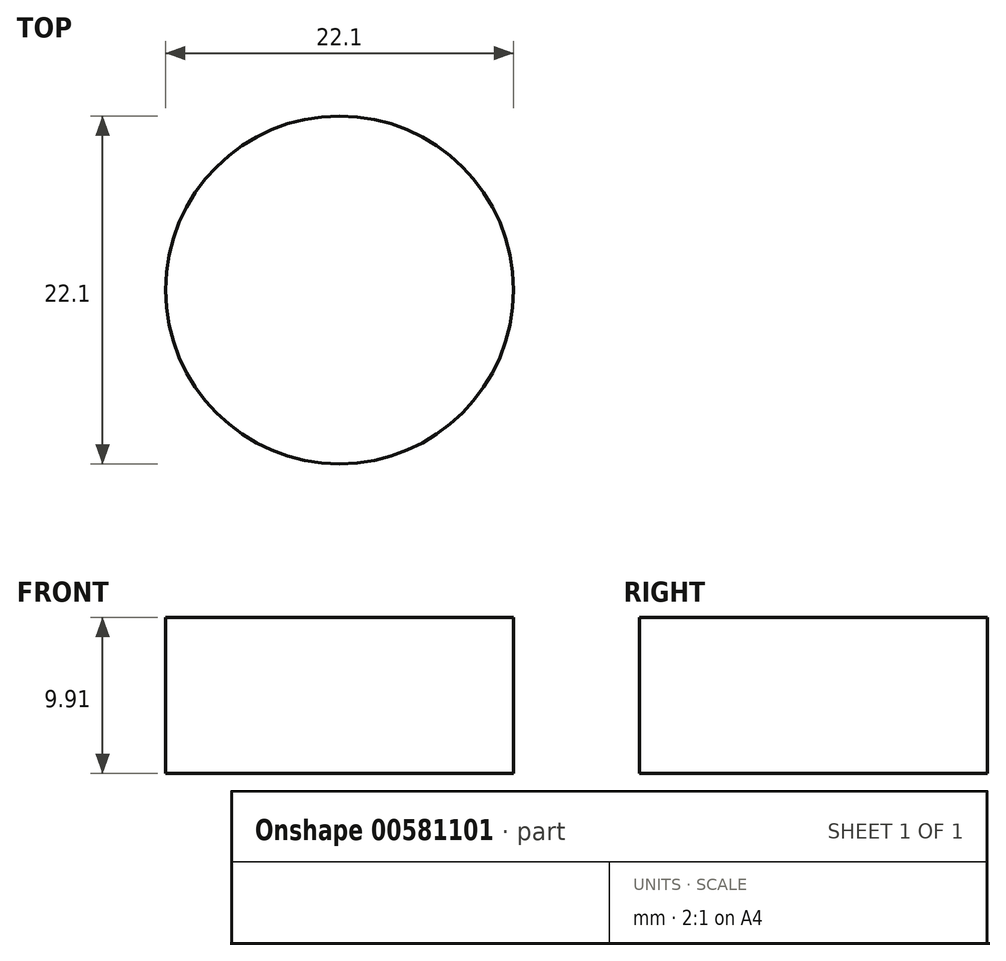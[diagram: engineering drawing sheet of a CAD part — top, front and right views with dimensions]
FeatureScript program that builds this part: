
annotation { "Feature Type Name" : "Feature", "Feature Type Description" : "" }
export const myFeature = defineFeature(function(context is Context, id is Id, definition is map)
    precondition{}
    {
        {
            var Q0;
            Q0=qCreatedBy(makeId("Top.planeOp"),FACE);
            var sketch = newSketch(context, id + "F0", { "sketchPlane" : qUnion([Q0])});
            skCircle(sketch, "E0", {"center": v(-31.9, 20.82) * mm, "radius": 11.05 * mm});
            skCircle(sketch, "E1", {"center": v(-40.08, 41.81) * mm, "radius": 11.05 * mm});
            skCircle(sketch, "E2", {"center": v(-9.4, 20.82) * mm, "radius": 11.05 * mm});
            skCircle(sketch, "E3", {"center": v(-44.48, 2.52) * mm, "radius": 11.05 * mm});
            skSolve(sketch);
        }
        {
            var Q0;
            Q0=makeQuery(id+"F0.imprint","IMPRINT",FACE,{"disambiguationData":[TD([[makeQuery(id+"F0.imprint","IMPRINT",EDGE,{"derivedFrom":sQuery(id+"F0.wireOp",EDGE,"E1")}),1.0]])]});
            extrude(context, id + "F1", {"entities" : qUnion([Q0]), "depth" : 9.9 * mm, "offsetDistance" : 25.4 * mm});
        }
    });
